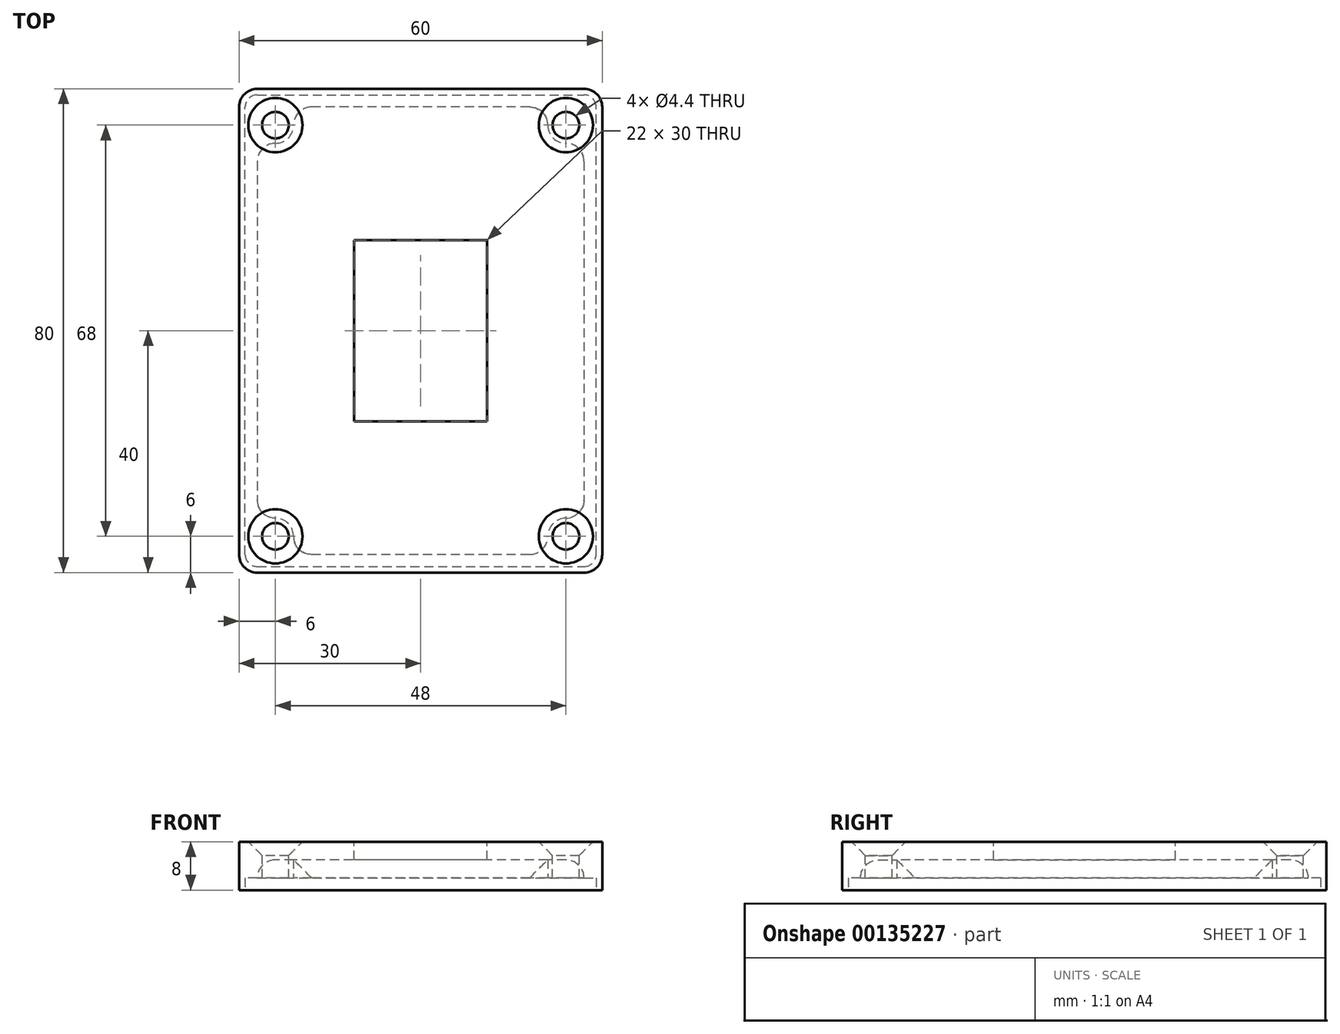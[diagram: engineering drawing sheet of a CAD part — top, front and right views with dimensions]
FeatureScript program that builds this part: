
annotation { "Feature Type Name" : "Feature", "Feature Type Description" : "" }
export const myFeature = defineFeature(function(context is Context, id is Id, definition is map)
    precondition{}
    {
        {
            var Q0;
            Q0=qCreatedBy(makeId("Top.planeOp"),FACE);
            var sketch = newSketch(context, id + "F0", { "sketchPlane" : qUnion([Q0])});
            skLineSegment(sketch, "E0.bottom", {"start": v(30, -40) * mm, "end": v(-30, -40) * mm});
            skLineSegment(sketch, "E0.top", {"start": v(30, 40) * mm, "end": v(-30, 40) * mm});
            skLineSegment(sketch, "E0.left", {"start": v(30, -40) * mm, "end": v(30, 40) * mm});
            skLineSegment(sketch, "E0.right", {"start": v(-30, -40) * mm, "end": v(-30, 40) * mm});
            skPoint(sketch, "E0.middle", {"position": v(0, 0) * mm});
            skSolve(sketch);
        }
        {
            var Q0;
            Q0=makeQuery(id+"F0.imprint","IMPRINT",FACE,{"disambiguationData":[TD([[makeQuery(id+"F0.imprint","IMPRINT",EDGE,{"derivedFrom":sQuery(id+"F0.wireOp",EDGE,"E0.bottom")}),-1.0]])]});
            extrude(context, id + "F1", {"entities" : qUnion([Q0]), "depth" : 8 * mm});
        }
        {
            var Q0;
            Q0=makeQuery(id+"F1.opExtrude","CAP_FACE",FACE,{"disambiguationData":[OSD([sQuery(id+"F0.wireOp",EDGE,"E0.bottom"),sQuery(id+"F0.wireOp",EDGE,"E0.top"),sQuery(id+"F0.wireOp",EDGE,"E0.left"),sQuery(id+"F0.wireOp",EDGE,"E0.right")])],"isStart":true});
            var sketch = newSketch(context, id + "F2", { "sketchPlane" : qUnion([Q0])});
            skLineSegment(sketch, "E1.bottom", {"start": v(27, -37) * mm, "end": v(-27, -37) * mm});
            skLineSegment(sketch, "E1.top", {"start": v(27, 37) * mm, "end": v(-27, 37) * mm});
            skLineSegment(sketch, "E1.left", {"start": v(27, -37) * mm, "end": v(27, 37) * mm});
            skLineSegment(sketch, "E1.right", {"start": v(-27, -37) * mm, "end": v(-27, 37) * mm});
            skPoint(sketch, "E1.middle", {"position": v(0, 0) * mm});
            skArc(sketch, "E2", {"start": v(-24, 31) * mm, "mid": v(-21.88, 31.88) * mm, "end": v(-21, 34) * mm});
            skArc(sketch, "E3", {"start": v(21, 34) * mm, "mid": v(21.88, 31.88) * mm, "end": v(24, 31) * mm});
            skArc(sketch, "E4", {"start": v(24, -31) * mm, "mid": v(21.88, -31.88) * mm, "end": v(21, -34) * mm});
            skArc(sketch, "E5", {"start": v(-21, -34) * mm, "mid": v(-21.88, -31.88) * mm, "end": v(-24, -31) * mm});
            skLineSegment(sketch, "E6", {"start": v(-24, -31) * mm, "end": v(-27, -31) * mm});
            skLineSegment(sketch, "E7", {"start": v(-21, -34) * mm, "end": v(-21, -37) * mm});
            skLineSegment(sketch, "E8", {"start": v(21, -34) * mm, "end": v(21, -37) * mm});
            skLineSegment(sketch, "E9", {"start": v(24, -31) * mm, "end": v(27, -31) * mm});
            skLineSegment(sketch, "E10", {"start": v(-24, 31) * mm, "end": v(-27, 31) * mm});
            skLineSegment(sketch, "E11", {"start": v(-21, 34) * mm, "end": v(-21, 37) * mm});
            skLineSegment(sketch, "E12", {"start": v(21, 34) * mm, "end": v(21, 37) * mm});
            skLineSegment(sketch, "E13", {"start": v(24, 31) * mm, "end": v(27, 31) * mm});
            skSolve(sketch);
        }
        {
            var Q0;
            Q0=makeQuery(id+"F2.imprint","IMPRINT",FACE,{"disambiguationData":[TD([[makeQuery(id+"F2.imprint","IMPRINT",EDGE,{"derivedFrom":sQuery(id+"F2.wireOp",EDGE,"E2")}),-1.0]])]});
            extrude(context, id + "F3", {"entities" : qUnion([Q0]), "operationType" : NewBodyOperationType.REMOVE, "oppositeDirection" : true, "depth" : 5 * mm});
        }
        {
            var Q0;
            Q0=makeQuery(id+"F3.boolean.opBoolean","COPY",EDGE,{"derivedFrom":makeQuery(id+"F3.opExtrude","CAP_EDGE",EDGE,{"disambiguationData":[OSD([sQuery(id+"F2.wireOp",EDGE,"E1.top")])],"isStart":false})});
            var Q1;
            Q1=makeQuery(id+"F3.boolean.opBoolean","COPY",EDGE,{"derivedFrom":makeQuery(id+"F3.opExtrude","CAP_EDGE",EDGE,{"disambiguationData":[OSD([sQuery(id+"F2.wireOp",EDGE,"E1.right")])],"isStart":false})});
            var Q2;
            Q2=makeQuery(id+"F3.boolean.opBoolean","COPY",EDGE,{"derivedFrom":makeQuery(id+"F3.opExtrude","CAP_EDGE",EDGE,{"disambiguationData":[OSD([sQuery(id+"F2.wireOp",EDGE,"E1.left")])],"isStart":false})});
            var Q3;
            Q3=makeQuery(id+"F3.boolean.opBoolean","COPY",EDGE,{"derivedFrom":makeQuery(id+"F3.opExtrude","SWEPT_EDGE",EDGE,{"disambiguationData":[OSD([sQuery(id+"F2.wireOp",EDGE,"E1.bottom"),sQuery(id+"F2.wireOp",EDGE,"E1.left")])]})});
            var Q4;
            Q4=makeQuery(id+"F3.boolean.opBoolean","COPY",EDGE,{"derivedFrom":makeQuery(id+"F3.opExtrude","SWEPT_EDGE",EDGE,{"disambiguationData":[OSD([sQuery(id+"F2.wireOp",EDGE,"E1.bottom"),sQuery(id+"F2.wireOp",EDGE,"E1.right")])]})});
            var Q5;
            Q5=makeQuery(id+"F1.opExtrude","SWEPT_EDGE",EDGE,{"disambiguationData":[OSD([sQuery(id+"F0.wireOp",EDGE,"E0.bottom"),sQuery(id+"F0.wireOp",EDGE,"E0.right")])]});
            var Q6;
            Q6=makeQuery(id+"F1.opExtrude","SWEPT_EDGE",EDGE,{"disambiguationData":[OSD([sQuery(id+"F0.wireOp",EDGE,"E0.top"),sQuery(id+"F0.wireOp",EDGE,"E0.right")])]});
            var Q7;
            Q7=makeQuery(id+"F1.opExtrude","SWEPT_EDGE",EDGE,{"disambiguationData":[OSD([sQuery(id+"F0.wireOp",EDGE,"E0.top"),sQuery(id+"F0.wireOp",EDGE,"E0.left")])]});
            var Q8;
            Q8=makeQuery(id+"F1.opExtrude","SWEPT_EDGE",EDGE,{"disambiguationData":[OSD([sQuery(id+"F0.wireOp",EDGE,"E0.bottom"),sQuery(id+"F0.wireOp",EDGE,"E0.left")])]});
            var Q9;
            Q9=makeQuery(id+"F3.boolean.opBoolean","COPY",EDGE,{"derivedFrom":makeQuery(id+"F3.opExtrude","SWEPT_EDGE",EDGE,{"disambiguationData":[OSD([sQuery(id+"F2.wireOp",EDGE,"E1.top"),sQuery(id+"F2.wireOp",EDGE,"E1.right")])]})});
            var Q10;
            Q10=makeQuery(id+"F3.boolean.opBoolean","COPY",EDGE,{"derivedFrom":makeQuery(id+"F3.opExtrude","SWEPT_EDGE",EDGE,{"disambiguationData":[OSD([sQuery(id+"F2.wireOp",EDGE,"E1.top"),sQuery(id+"F2.wireOp",EDGE,"E1.left")])]})});
            var Q11;
            Q11=makeQuery(id+"F3.boolean.opBoolean","COPY",EDGE,{"derivedFrom":makeQuery(id+"F3.opExtrude","CAP_EDGE",EDGE,{"disambiguationData":[OSD([sQuery(id+"F2.wireOp",EDGE,"E1.bottom")])],"isStart":false})});
            fillet(context, id + "F4", {"entities" : qUnion([Q0, Q1, Q2, Q3, Q4, Q5, Q6, Q7, Q8, Q9, Q10, Q11]), "radius" : 3 * mm, "tangentPropagation" : true, "allowEdgeOverflow" : false});
        }
        {
            var Q0;
            Q0=makeQuery(id+"F1.opExtrude","CAP_FACE",FACE,{"disambiguationData":[OSD([sQuery(id+"F0.wireOp",EDGE,"E0.bottom"),sQuery(id+"F0.wireOp",EDGE,"E0.top"),sQuery(id+"F0.wireOp",EDGE,"E0.left"),sQuery(id+"F0.wireOp",EDGE,"E0.right")])],"isStart":false});
            var sketch = newSketch(context, id + "F5", { "sketchPlane" : qUnion([Q0])});
            skLineSegment(sketch, "E14.bottom", {"start": v(24, -34) * mm, "end": v(-24, -34) * mm});
            skLineSegment(sketch, "E14.top", {"start": v(24, 34) * mm, "end": v(-24, 34) * mm});
            skLineSegment(sketch, "E14.left", {"start": v(24, -34) * mm, "end": v(24, 34) * mm});
            skLineSegment(sketch, "E14.right", {"start": v(-24, -34) * mm, "end": v(-24, 34) * mm});
            skPoint(sketch, "E14.middle", {"position": v(0, 0) * mm});
            skSolve(sketch);
        }
        {
            var Q0;
            Q0=sQuery(id+"F5.wireOp",VERTEX,"E14.right.end");
            var Q1;
            Q1=sQuery(id+"F5.wireOp",VERTEX,"E14.left.end");
            var Q2;
            Q2=sQuery(id+"F5.wireOp",VERTEX,"E14.bottom.start");
            var Q3;
            Q3=sQuery(id+"F5.wireOp",VERTEX,"E14.right.start");
            var Q4;
            Q4=makeQuery(id+"F1.opExtrude","SWEPT_BODY",BODY,{"disambiguationData":[OSD([sQuery(id+"F0.wireOp",EDGE,"E0.bottom"),sQuery(id+"F0.wireOp",EDGE,"E0.top"),sQuery(id+"F0.wireOp",EDGE,"E0.left"),sQuery(id+"F0.wireOp",EDGE,"E0.right")])]});
            hole(context, id + "F6", {"style" : HoleStyle.C_SINK, "endStyle" : HoleEndStyle.THROUGH, "standardTappedOrClearance" : lookupTablePath({ "standard" : "ISO", "fit" : "Normal", "size" : "M4", "type" : "Clearance" }), "standardBlindInLast" : lookupTablePath({ "fit" : "Standard", "standard" : "ISO", "size" : "M4", "type" : "Clearance" }), "holeDiameter" : 4.4 * mm, "cSinkDiameter" : 8.96 * mm, "cSinkAngle" : 90 * degree, "isTappedThrough" : true, "tappedDepth" : 12 * mm, "tapClearance" : 3, "locations" : qUnion([Q0, Q1, Q2, Q3]), "scope" : qUnion([Q4])});
        }
        {
            var Q0;
            Q0=makeQuery(id+"F1.opExtrude","CAP_FACE",FACE,{"disambiguationData":[OSD([sQuery(id+"F0.wireOp",EDGE,"E0.bottom"),sQuery(id+"F0.wireOp",EDGE,"E0.top"),sQuery(id+"F0.wireOp",EDGE,"E0.left"),sQuery(id+"F0.wireOp",EDGE,"E0.right")])],"isStart":false});
            var sketch = newSketch(context, id + "F7", { "sketchPlane" : qUnion([Q0])});
            skLineSegment(sketch, "E15.bottom", {"start": v(11, -15) * mm, "end": v(-11, -15) * mm});
            skLineSegment(sketch, "E15.top", {"start": v(11, 15) * mm, "end": v(-11, 15) * mm});
            skLineSegment(sketch, "E15.left", {"start": v(11, -15) * mm, "end": v(11, 15) * mm});
            skLineSegment(sketch, "E15.right", {"start": v(-11, -15) * mm, "end": v(-11, 15) * mm});
            skPoint(sketch, "E15.middle", {"position": v(0, 0) * mm});
            skSolve(sketch);
        }
        {
            var Q0;
            Q0=makeQuery(id+"F7.imprint","IMPRINT",FACE,{"disambiguationData":[TD([[makeQuery(id+"F7.imprint","IMPRINT",EDGE,{"derivedFrom":sQuery(id+"F7.wireOp",EDGE,"MmbnlgV6-smly-AmUU-TsuR-TWUZMVt3VpDt")}),1.0]])]});
            var Q1;
            Q1=makeQuery(id+"F7.imprint","IMPRINT",FACE,{"disambiguationData":[TD([[makeQuery(id+"F7.imprint","IMPRINT",EDGE,{"derivedFrom":sQuery(id+"F7.wireOp",EDGE,"E15.bottom")}),-1.0]])]});
            extrude(context, id + "F8", {"entities" : qUnion([Q0, Q1]), "operationType" : NewBodyOperationType.REMOVE, "endBound" : BoundingType.UP_TO_NEXT, "oppositeDirection" : true, "depth" : 25 * mm});
        }
        {
            var Q0;
            Q0=makeQuery(id+"F1.opExtrude","CAP_FACE",FACE,{"disambiguationData":[OSD([sQuery(id+"F0.wireOp",EDGE,"E0.bottom"),sQuery(id+"F0.wireOp",EDGE,"E0.top"),sQuery(id+"F0.wireOp",EDGE,"E0.left"),sQuery(id+"F0.wireOp",EDGE,"E0.right")])],"isStart":true});
            var sketch = newSketch(context, id + "F9", { "sketchPlane" : qUnion([Q0])});
            skLineSegment(sketch, "E16.bottom", {"start": v(-29, 39) * mm, "end": v(29, 39) * mm});
            skLineSegment(sketch, "E16.top", {"start": v(-29, -39) * mm, "end": v(29, -39) * mm});
            skLineSegment(sketch, "E16.left", {"start": v(-29, 39) * mm, "end": v(-29, -39) * mm});
            skLineSegment(sketch, "E16.right", {"start": v(29, 39) * mm, "end": v(29, -39) * mm});
            skPoint(sketch, "E16.middle", {"position": v(0, 0) * mm});
            skSolve(sketch);
        }
        {
            var Q0;
            Q0=makeQuery(id+"F9.imprint","IMPRINT",FACE,{"disambiguationData":[TD([[makeQuery(id+"F9.imprint","IMPRINT",EDGE,{"derivedFrom":sQuery(id+"F9.wireOp",EDGE,"E16.bottom")}),-1.0]])]});
            extrude(context, id + "F10", {"entities" : qUnion([Q0]), "operationType" : NewBodyOperationType.REMOVE, "oppositeDirection" : true, "depth" : 2 * mm});
        }
        {
            var Q0;
            Q0=makeQuery(id+"F10.boolean.opBoolean","COPY",EDGE,{"derivedFrom":makeQuery(id+"F10.opExtrude","SWEPT_EDGE",EDGE,{"disambiguationData":[OSD([sQuery(id+"F9.wireOp",EDGE,"E16.top"),sQuery(id+"F9.wireOp",EDGE,"E16.left")])]})});
            var Q1;
            Q1=makeQuery(id+"F10.boolean.opBoolean","COPY",EDGE,{"derivedFrom":makeQuery(id+"F10.opExtrude","SWEPT_EDGE",EDGE,{"disambiguationData":[OSD([sQuery(id+"F9.wireOp",EDGE,"E16.bottom"),sQuery(id+"F9.wireOp",EDGE,"E16.left")])]})});
            var Q2;
            Q2=makeQuery(id+"F10.boolean.opBoolean","COPY",EDGE,{"derivedFrom":makeQuery(id+"F10.opExtrude","SWEPT_EDGE",EDGE,{"disambiguationData":[OSD([sQuery(id+"F9.wireOp",EDGE,"E16.bottom"),sQuery(id+"F9.wireOp",EDGE,"E16.right")])]})});
            var Q3;
            Q3=makeQuery(id+"F10.boolean.opBoolean","COPY",EDGE,{"derivedFrom":makeQuery(id+"F10.opExtrude","SWEPT_EDGE",EDGE,{"disambiguationData":[OSD([sQuery(id+"F9.wireOp",EDGE,"E16.top"),sQuery(id+"F9.wireOp",EDGE,"E16.right")])]})});
            fillet(context, id + "F11", {"entities" : qUnion([Q0, Q1, Q2, Q3]), "radius" : 2 * mm, "tangentPropagation" : true, "allowEdgeOverflow" : false});
        }
    });
